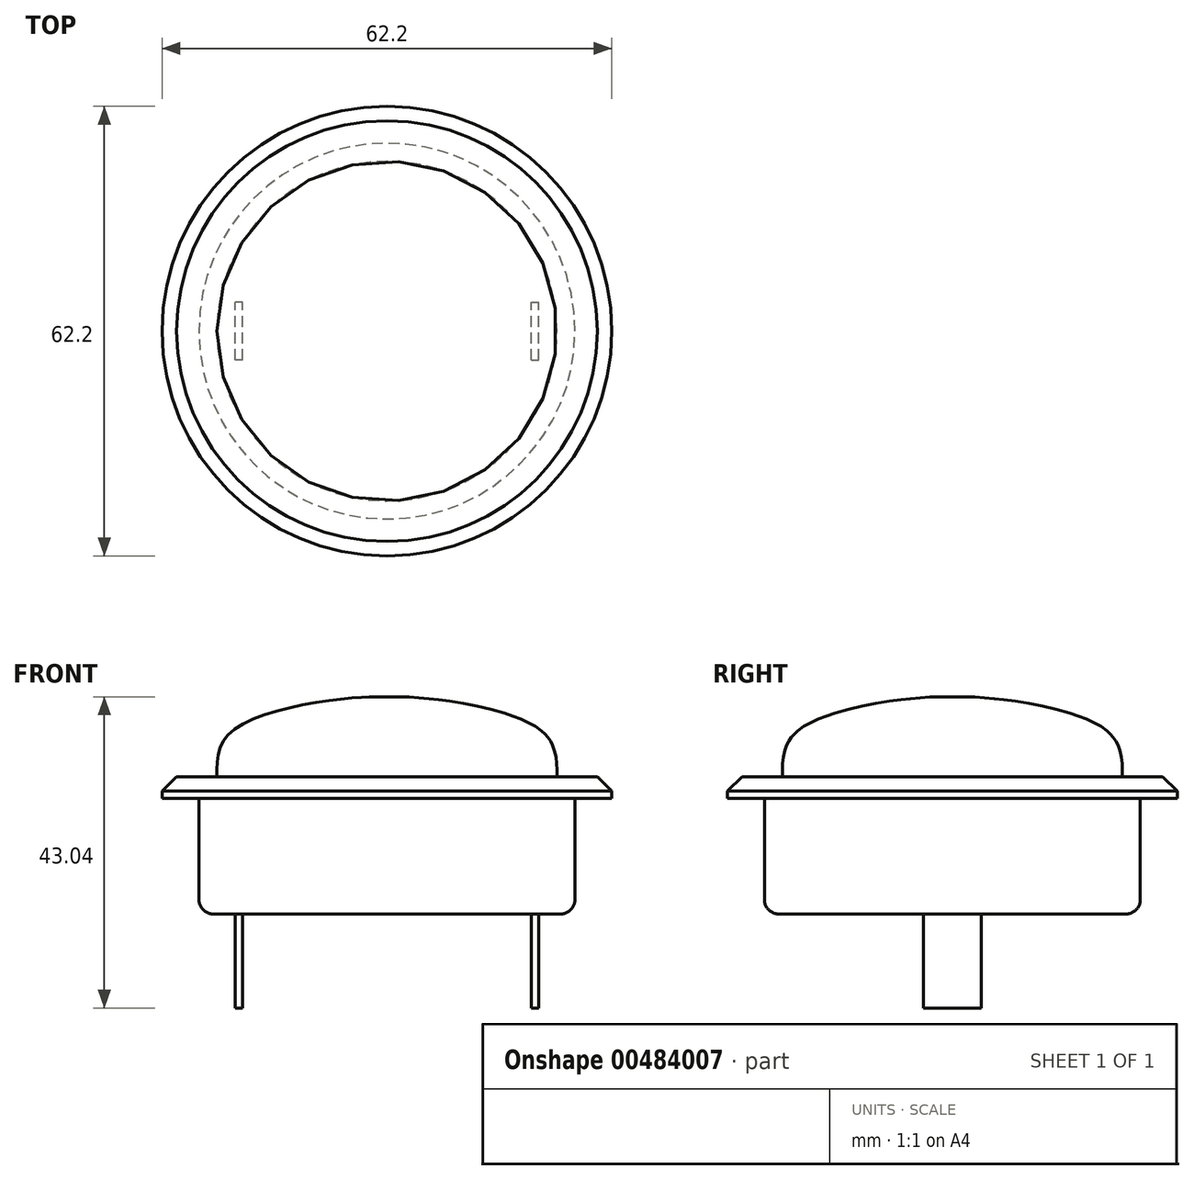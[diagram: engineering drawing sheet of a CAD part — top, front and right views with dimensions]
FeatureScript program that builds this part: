
annotation { "Feature Type Name" : "Feature", "Feature Type Description" : "" }
export const myFeature = defineFeature(function(context is Context, id is Id, definition is map)
    precondition{}
    {
        {
            var Q0;
            Q0=qCreatedBy(makeId("Top.planeOp"),FACE);
            var sketch = newSketch(context, id + "F0", { "sketchPlane" : qUnion([Q0])});
            skCircle(sketch, "E0", {"center": v(0, 0) * mm, "radius": 31.1 * mm});
            skSolve(sketch);
        }
        {
            var Q0;
            Q0=makeQuery(id+"F0.imprint","IMPRINT",FACE,{"disambiguationData":[TD([[makeQuery(id+"F0.imprint","IMPRINT",EDGE,{"derivedFrom":sQuery(id+"F0.wireOp",EDGE,"E0")}),1.0]])]});
            var Q1;
            Q1=sQuery(id+"F0.wireOp",EDGE,"E0");
            extrude(context, id + "F1", {"entities" : qUnion([Q0]), "surfaceEntities" : qUnion([Q1]), "depth" : 3 * mm});
        }
        {
            var Q0;
            Q0=makeQuery(id+"F1.opExtrude","CAP_EDGE",EDGE,{"disambiguationData":[OSD([sQuery(id+"F0.wireOp",EDGE,"E0")])],"isStart":false});
            chamfer(context, id + "F2", {"entities" : qUnion([Q0]), "width" : 2 * mm, "tangentPropagation" : true});
        }
        {
            var Q0;
            Q0=makeQuery(id+"F1.opExtrude","CAP_FACE",FACE,{"disambiguationData":[OSD([sQuery(id+"F0.wireOp",EDGE,"E0")])],"isStart":true});
            var sketch = newSketch(context, id + "F3", { "sketchPlane" : qUnion([Q0])});
            skCircle(sketch, "E1", {"center": v(0, 0) * mm, "radius": 26 * mm});
            skSolve(sketch);
        }
        {
            var Q0;
            Q0 = qSketchRegion(id + "F3", true);
            extrude(context, id + "F4", {"entities" : qUnion([Q0]), "operationType" : NewBodyOperationType.ADD, "depth" : 16 * mm});
        }
        {
            var Q0;
            Q0=makeQuery(id+"F4.opExtrude","CAP_EDGE",EDGE,{"disambiguationData":[OSD([sQuery(id+"F3.wireOp",EDGE,"E1")])],"isStart":false});
            fillet(context, id + "F5", {"entities" : qUnion([Q0]), "radius" : 2 * mm, "tangentPropagation" : true, "allowEdgeOverflow" : false});
        }
        {
            var Q0;
            Q0=makeQuery(id+"F4.opExtrude","CAP_FACE",FACE,{"disambiguationData":[OSD([sQuery(id+"F3.wireOp",EDGE,"E1")])],"isStart":false});
            var sketch = newSketch(context, id + "F6", { "sketchPlane" : qUnion([Q0])});
            skPoint(sketch, "E2.0", {"position": v(0, 0) * mm});
            skLineSegment(sketch, "E3", {"start": v(0, 0) * mm, "end": v(-20.5, 0) * mm, "construction": true});
            skLineSegment(sketch, "E4.bottom", {"start": v(-20, 4) * mm, "end": v(-21, 4) * mm});
            skLineSegment(sketch, "E4.top", {"start": v(-20, -4) * mm, "end": v(-21, -4) * mm});
            skLineSegment(sketch, "E4.left", {"start": v(-20, 4) * mm, "end": v(-20, -4) * mm});
            skLineSegment(sketch, "E4.right", {"start": v(-21, 4) * mm, "end": v(-21, -4) * mm});
            skPoint(sketch, "E4.middle", {"position": v(-20.5, 0) * mm});
            skCircle(sketch, "E5.0", {"center": v(0, 0) * mm, "radius": 26 * mm});
            skPoint(sketch, "E6.MirrorP", {"position": v(20.5, 0) * mm});
            skLineSegment(sketch, "E7.MirrorCS", {"start": v(20, 4) * mm, "end": v(21, 4) * mm});
            skLineSegment(sketch, "E8.MirrorCS", {"start": v(20, 4) * mm, "end": v(20, -4) * mm});
            skLineSegment(sketch, "E9.MirrorCS", {"start": v(20, -4) * mm, "end": v(21, -4) * mm});
            skLineSegment(sketch, "E10.MirrorCS", {"start": v(21, 4) * mm, "end": v(21, -4) * mm});
            skSolve(sketch);
        }
        {
            var Q0;
            Q0=makeQuery(id+"F6.imprint","IMPRINT",FACE,{"disambiguationData":[TD([[makeQuery(id+"F6.imprint","IMPRINT",EDGE,{"derivedFrom":sQuery(id+"F6.wireOp",EDGE,"E4.bottom")}),1.0]])]});
            var Q1;
            Q1=makeQuery(id+"F6.imprint","IMPRINT",FACE,{"disambiguationData":[TD([[makeQuery(id+"F6.imprint","IMPRINT",EDGE,{"derivedFrom":sQuery(id+"F6.wireOp",EDGE,"E7.MirrorCS")}),-1.0]])]});
            extrude(context, id + "F7", {"entities" : qUnion([Q0, Q1]), "operationType" : NewBodyOperationType.ADD, "depth" : 13 * mm});
        }
        {
            var Q0;
            Q0=makeQuery(id+"F1.opExtrude","CAP_FACE",FACE,{"disambiguationData":[OSD([sQuery(id+"F0.wireOp",EDGE,"E0")])],"isStart":false});
            var sketch = newSketch(context, id + "F8", { "sketchPlane" : qUnion([Q0])});
            skPoint(sketch, "E11.0", {"position": v(0, 0) * mm});
            skCircle(sketch, "E12", {"center": v(0, 0) * mm, "radius": 23.5 * mm});
            skSolve(sketch);
        }
        {
            var Q0;
            Q0=qCreatedBy(makeId("Front.planeOp"),FACE);
            var sketch = newSketch(context, id + "F9", { "sketchPlane" : qUnion([Q0])});
            skLineSegment(sketch, "E13", {"start": v(0, 0) * mm, "end": v(0, 15) * mm});
            skLineSegment(sketch, "E14.0", {"start": v(-23.5, 14) * mm, "end": v(23.5, 14) * mm, "construction": true});
            skLineSegment(sketch, "E15", {"start": v(-23.5, 14) * mm, "end": v(-23.5, 3) * mm, "construction": true});
            skFitSpline(sketch, "E16", {"points": [v(-23.5, 3) * mm, v(-21.14, 9.53) * mm, v(-3.25, 14) * mm, v(0, 14) * mm], "startDerivative": vector(-0.44, 23.33) * mm, "endDerivative": vector(8.63, 0) * mm});
            skLineSegment(sketch, "E17", {"start": v(-23.5, 3) * mm, "end": v(0, 3) * mm});
            skLineSegment(sketch, "E18", {"start": v(0, 3) * mm, "end": v(0, 14) * mm});
            skSolve(sketch);
        }
        {
            var Q0;
            Q0=makeQuery(id+"F9.imprint","IMPRINT",FACE,{"disambiguationData":[TD([[makeQuery(id+"F9.imprint","IMPRINT",EDGE,{"derivedFrom":sQuery(id+"F9.wireOp",EDGE,"E16")}),-1.0]])]});
            var Q1;
            Q1=sQuery(id+"F9.wireOp",EDGE,"E18");
            revolve(context, id + "F10", {"operationType" : NewBodyOperationType.ADD, "entities" : qUnion([Q0]), "axis" : qUnion([Q1]), "revolveType" : RevolveType.FULL});
        }
    });
